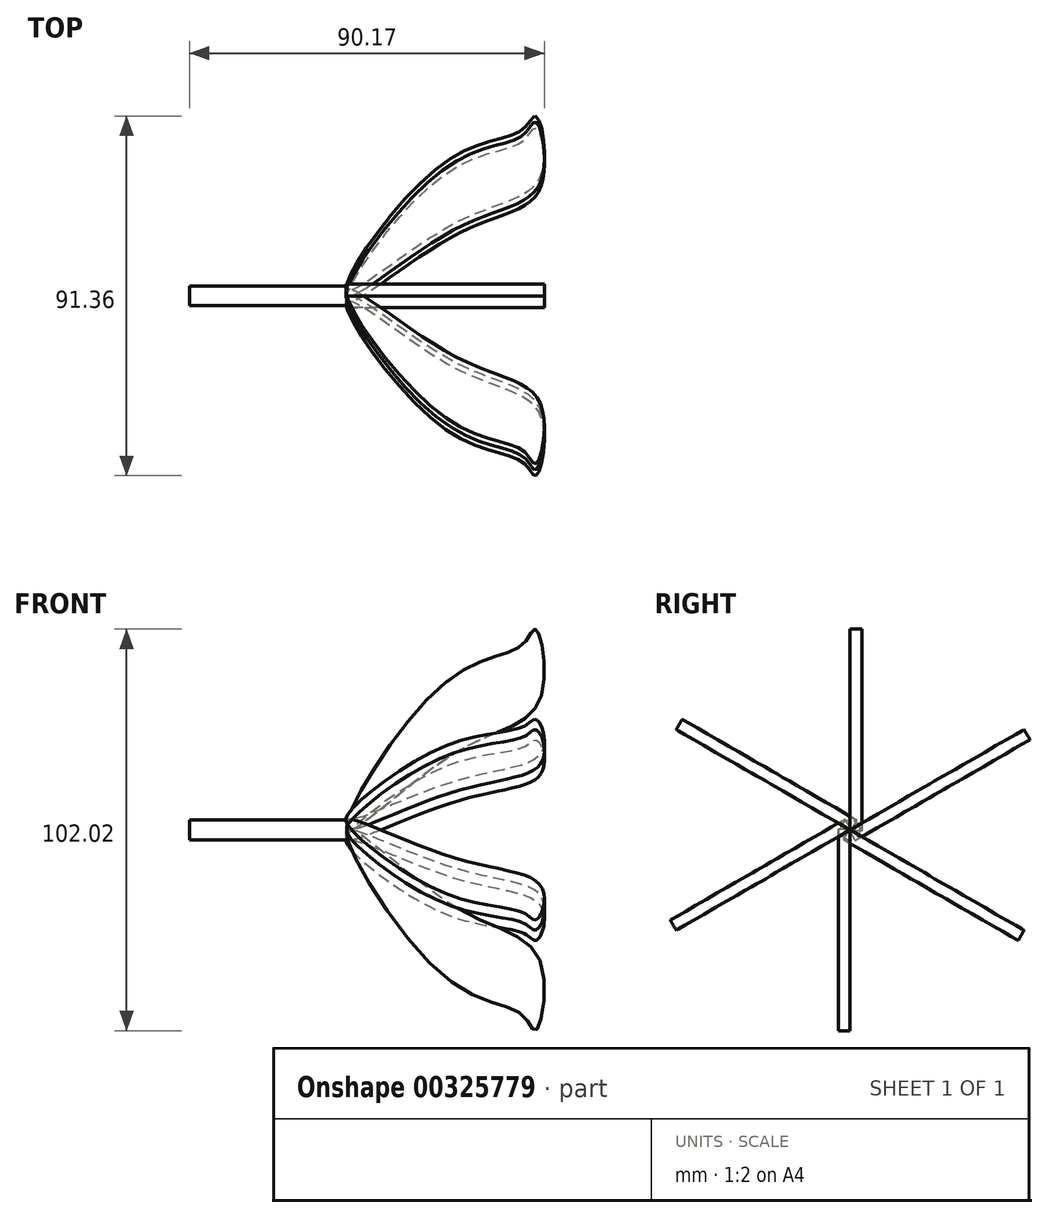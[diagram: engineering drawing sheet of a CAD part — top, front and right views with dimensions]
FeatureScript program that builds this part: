
annotation { "Feature Type Name" : "Feature", "Feature Type Description" : "" }
export const myFeature = defineFeature(function(context is Context, id is Id, definition is map)
    precondition{}
    {
        {
            var Q0;
            Q0=qCreatedBy(makeId("Front.planeOp"),FACE);
            var sketch = newSketch(context, id + "F0", { "sketchPlane" : qUnion([Q0])});
            skFitSpline(sketch, "E0", {"points": [v(0, 0) * mm, v(25.58, 37.94) * mm, v(44.9, 47.32) * mm, v(47.97, 50.98) * mm, v(49.17, 33.4) * mm, v(27.85, 19.75) * mm, v(0, 0) * mm]});
            skFitSpline(sketch, "E1.0", {"points": [v(-1.27, -1.99) * mm, v(-1.77, -1.48) * mm, v(-2.05, -1.04) * mm, v(-2.25, -0.61) * mm, v(-2.4, -0.11) * mm, v(-2.46, 0.42) * mm, v(-2.46, 0.9) * mm, v(-2.42, 1.37) * mm, v(-2.32, 1.98) * mm, v(-2.14, 2.74) * mm, v(-1.83, 3.73) * mm, v(-1.44, 4.78) * mm, v(-0.96, 5.91) * mm, v(-0.23, 7.53) * mm, v(0.88, 9.73) * mm, v(2.48, 12.62) * mm, v(4.31, 15.7) * mm, v(6.36, 18.92) * mm, v(8.58, 22.2) * mm, v(11.73, 26.56) * mm, v(15.1, 30.8) * mm, v(18.6, 34.64) * mm, v(20.8, 36.83) * mm, v(22.56, 38.42) * mm, v(23.88, 39.53) * mm, v(25.2, 40.54) * mm, v(26.94, 41.75) * mm, v(29.06, 43.02) * mm, v(31.5, 44.23) * mm, v(33.8, 45.17) * mm, v(35.95, 45.92) * mm, v(37.9, 46.54) * mm, v(39.6, 47.08) * mm, v(41.06, 47.6) * mm, v(42.02, 48.05) * mm, v(42.63, 48.41) * mm, v(42.95, 48.64) * mm, v(43.18, 48.83) * mm, v(43.33, 48.97) * mm, v(43.48, 49.13) * mm, v(43.68, 49.37) * mm, v(43.94, 49.72) * mm, v(44.25, 50.17) * mm, v(44.55, 50.66) * mm, v(44.85, 51.16) * mm, v(45.12, 51.59) * mm, v(45.37, 51.94) * mm, v(45.6, 52.22) * mm, v(45.9, 52.52) * mm, v(46.29, 52.85) * mm, v(46.78, 53.11) * mm, v(47.28, 53.26) * mm, v(47.71, 53.31) * mm, v(48.16, 53.3) * mm, v(48.6, 53.2) * mm, v(48.99, 53.04) * mm, v(49.3, 52.85) * mm, v(49.57, 52.66) * mm, v(49.85, 52.4) * mm, v(50.12, 52.08) * mm, v(50.37, 51.72) * mm, v(50.57, 51.35) * mm, v(50.75, 50.98) * mm, v(50.96, 50.47) * mm, v(51.2, 49.79) * mm, v(51.46, 48.89) * mm, v(51.7, 47.9) * mm, v(51.9, 46.84) * mm, v(52.08, 45.72) * mm, v(52.28, 44.14) * mm, v(52.44, 42.04) * mm, v(52.48, 39.44) * mm, v(52.33, 37.26) * mm, v(52.1, 35.56) * mm, v(51.84, 34.32) * mm, v(51.5, 33.11) * mm, v(50.94, 31.57) * mm, v(50, 29.83) * mm, v(48.56, 28.08) * mm, v(46.88, 26.63) * mm, v(44.41, 25.03) * mm, v(41.68, 23.74) * mm, v(38.72, 22.49) * mm, v(36.4, 21.5) * mm, v(33.99, 20.43) * mm, v(31.9, 19.4) * mm, v(30.2, 18.47) * mm, v(28.9, 17.72) * mm, v(27.57, 16.9) * mm, v(25.77, 15.72) * mm, v(23.48, 14.1) * mm, v(20.7, 12.03) * mm, v(17.95, 9.86) * mm, v(15.27, 7.69) * mm, v(12.69, 5.56) * mm, v(10.26, 3.56) * mm, v(8.39, 2.05) * mm, v(7, 0.96) * mm, v(6, 0.21) * mm, v(5.08, -0.46) * mm, v(4.2, -1.06) * mm, v(3.38, -1.57) * mm, v(2.58, -2) * mm, v(1.9, -2.27) * mm, v(1.29, -2.44) * mm, v(0.77, -2.52) * mm, v(0.17, -2.52) * mm, v(-0.53, -2.37) * mm, v(-1.27, -1.99) * mm, v(-1.77, -1.48) * mm, v(-2.05, -1.04) * mm, v(-1.27, -1.99) * mm]});
            skLineSegment(sketch, "E2", {"start": v(0, 0) * mm, "end": v(47.97, 50.98) * mm, "construction": true});
            skSolve(sketch);
        }
        {
            var Q0;
            Q0=makeQuery(id+"F0.imprint","IMPRINT",FACE,{"disambiguationData":[TD([[makeQuery(id+"F0.imprint","IMPRINT",EDGE,{"derivedFrom":sQuery(id+"F0.wireOp",EDGE,"E0")}),-1.0]])]});
            extrude(context, id + "F1", {"entities" : qUnion([Q0]), "oppositeDirection" : true, "depth" : 3 * mm});
        }
        {
            var Q0;
            Q0=qCreatedBy(makeId("Front.planeOp"),FACE);
            var sketch = newSketch(context, id + "F2", { "sketchPlane" : qUnion([Q0])});
            skLineSegment(sketch, "E3", {"start": v(0, 0) * mm, "end": v(69.64, 0) * mm, "construction": true});
            skSolve(sketch);
        }
        {
            var Q0;
            Q0=makeQuery(id+"F1.opExtrude","SWEPT_BODY",BODY,{"disambiguationData":[OSD([sQuery(id+"F0.wireOp",EDGE,"E0")])]});
            var Q1;
            Q1=sQuery(id+"F2.wireOp",EDGE,"E3");
            circularPattern(context, id + "F3", {"entities" : qUnion([Q0]), "axis" : qUnion([Q1]), "angle" : 360 * degree, "instanceCount" : 6, "equalSpace" : true});
        }
        {
            var Q0;
            Q0=qCreatedBy(makeId("Front.planeOp"),FACE);
            var sketch = newSketch(context, id + "F4", { "sketchPlane" : qUnion([Q0])});
            skLineSegment(sketch, "E4.bottom", {"start": v(0, 0) * mm, "end": v(-40, 0) * mm});
            skLineSegment(sketch, "E4.top", {"start": v(0, 2.5) * mm, "end": v(-40, 2.5) * mm});
            skLineSegment(sketch, "E4.left", {"start": v(0, 0) * mm, "end": v(0, 2.5) * mm});
            skLineSegment(sketch, "E4.right", {"start": v(-40, 0) * mm, "end": v(-40, 2.5) * mm});
            skSolve(sketch);
        }
        {
            var Q0;
            Q0=makeQuery(id+"F4.imprint","IMPRINT",FACE,{"disambiguationData":[TD([[makeQuery(id+"F4.imprint","IMPRINT",EDGE,{"derivedFrom":sQuery(id+"F4.wireOp",EDGE,"E4.bottom")}),-1.0]])]});
            var Q1;
            Q1=sQuery(id+"F4.wireOp",EDGE,"E4.bottom");
            revolve(context, id + "F5", {"entities" : qUnion([Q0]), "axis" : qUnion([Q1]), "revolveType" : RevolveType.FULL});
        }
        {
            var Q0;
            Q0=qCreatedBy(makeId("Right.planeOp"),FACE);
            var sketch = newSketch(context, id + "F6", { "sketchPlane" : qUnion([Q0])});
            skCircle(sketch, "E5", {"center": v(0, 0) * mm, "radius": 3.07 * mm});
            skSolve(sketch);
        }
        {
            var Q0;
            Q0=sQuery(id+"F6.wireOp",EDGE,"E5");
            extrude(context, id + "F7", {"bodyType" : ToolBodyType.SURFACE, "surfaceEntities" : qUnion([Q0]), "depth" : 15 * mm});
        }
    });
